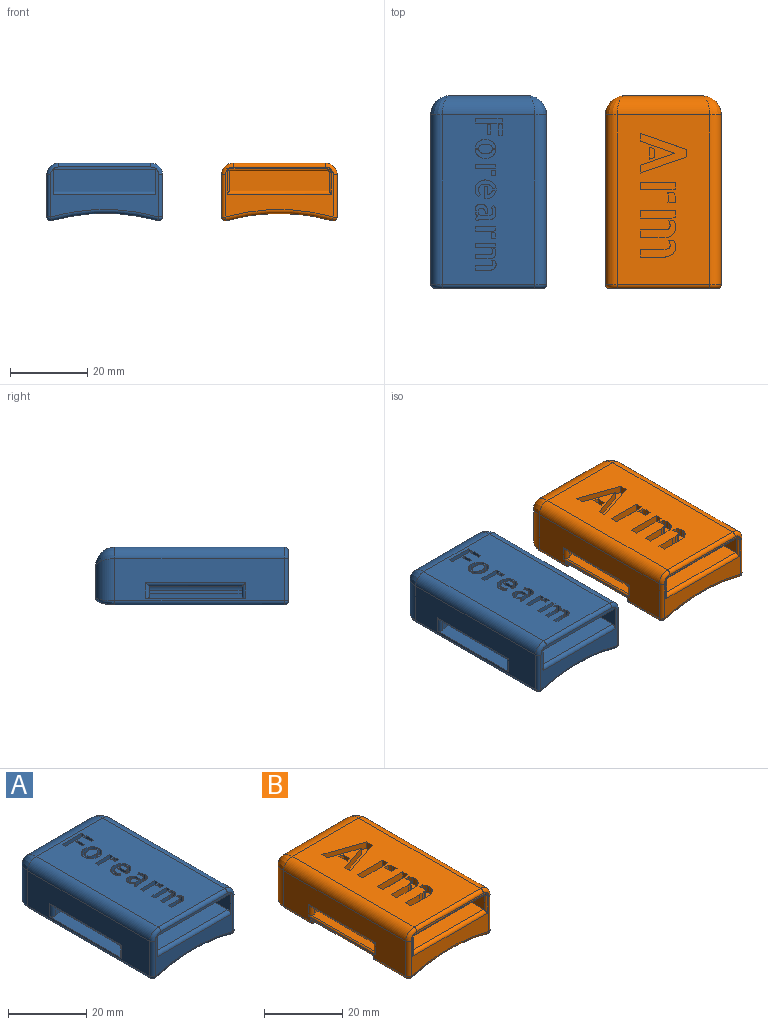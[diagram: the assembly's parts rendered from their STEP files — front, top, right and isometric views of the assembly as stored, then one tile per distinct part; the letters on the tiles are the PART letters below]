
ASSEMBLY  parts=2 mates=2
PART A: 261 faces, bbox 30.7x50x15.5 mm
  f0: cylinder r=50mm len=48mm, axis (0,1,0), area 1052.9mm2, adj f224,f227,f230,f231,f242,f243,f244,f245
  f1: cylinder r=50mm len=26mm, axis (0,1,0), area 125.4mm2, adj f5,f17,f18,f238,f239,f257
  f2: cylinder r=50mm len=24mm, axis (0,1,0), area 3.4mm2, adj f21,f22,f221,f259
  f3: plane 44x24mm, normal (0,0,1), area 969.2mm2, adj f7,f9,f23,f24,f25,f26,f27,f28
  f4: plane 45x26.5mm, normal (0,0,-1), area 1105.7mm2, adj f6,f11,f13,f14,f23,f24,f25,f26
  f5: plane 44x10.96mm, normal (1,0,0), area 375.8mm2, adj f1,f9,f230,f234,f238,f239,f240,f251
  f6: plane 28x12.96mm, normal (0,-1,0), area 152.2mm2, adj f4,f11,f13,f225,f226,f229,f231,f232
  f7: cylinder r=3mm len=44mm, axis (0,1,0), area 207.3mm2, adj f3,f8,f226,f254
  f8: plane 44x10.96mm, normal (-1,0,0), area 375.8mm2, adj f7,f20,f224,f225,f235,f236,f237,f255
  f9: cylinder r=3mm len=44mm, axis (0,1,0), area 207.3mm2, adj f3,f5,f232,f252
  f10: plane 20x7.99mm, normal (0,1,0), area 146.6mm2, adj f227,f251,f253,f255
  f11: plane 45x6.5mm, normal (1,0,0), area 247.7mm2, adj f4,f6,f12,f14,f241
  f12: plane 44x26.5mm, normal (0,0,1), area 1166mm2, adj f11,f13,f14,f241
  f13: plane 45x6.5mm, normal (-1,0,0), area 247.7mm2, adj f4,f6,f12,f14,f241
  f14: plane 26.5x5.5mm, normal (0,-1,0), area 145.7mm2, adj f4,f11,f12,f13
  f15: cylinder r=50mm len=24mm, axis (0,1,0), area 3.4mm2, adj f17,f18,f223,f260
  f16: cylinder r=50mm len=24mm, axis (0,1,0), area 146.8mm2, adj f17,f18,f240,f260
  f17: plane 9.64x4.49mm, normal (0,1,0), area 31mm2, adj f1,f15,f16,f222,f223,f238,f240,f244
  f18: plane 9.64x4.49mm, normal (0,-1,0), area 31mm2, adj f1,f15,f16,f222,f223,f239,f240,f242
  f19: cylinder r=50mm len=24mm, axis (0,1,0), area 146.8mm2, adj f21,f22,f237,f259
  f20: cylinder r=50mm len=26mm, axis (0,1,0), area 125.4mm2, adj f8,f21,f22,f235,f236,f258
  f21: plane 9.64x4.49mm, normal (0,1,0), area 31mm2, adj f2,f19,f20,f220,f221,f235,f237,f248
  f22: plane 9.64x4.49mm, normal (0,-1,0), area 31mm2, adj f2,f19,f20,f220,f221,f236,f237,f246
  f23: plane 1.75x0.55mm, normal (-0.22,0.98,0), area 1mm2, adj f3,f4,f24,f27
  f24: plane 1.75x1.03mm, normal (-1,0,0), area 1.8mm2, adj f3,f4,f23,f25
  f25: plane 5.36x1.75mm, normal (0,-1,0), area 9.4mm2, adj f3,f4,f24,f26
  f26: plane 1.75x1.16mm, normal (1,0,0), area 2mm2, adj f3,f4,f25,f27
  f27: plane 4.81x1.75mm, normal (0,1,0), area 8.4mm2, adj f3,f4,f23,f26
  f28: extruded ~1.75x0.61mm, area 1.1mm2, adj f3,f4,f29,f43
  f29: extruded ~1.75x0.49mm, area 0.9mm2, adj f3,f4,f28,f30
  f30: extruded ~1.75x0.52mm, area 1mm2, adj f3,f4,f29,f31
  f31: plane 1.75x0.75mm, normal (0,-1,0), area 1.3mm2, adj f3,f4,f30,f32
  f32: extruded ~1.75x0.5mm, area 0.9mm2, adj f3,f4,f31,f33
  f33: extruded ~1.75x0.29mm, area 0.5mm2, adj f3,f4,f32,f34
  f34: extruded ~1.75x0.39mm, area 0.7mm2, adj f3,f4,f33,f35
  f35: extruded ~1.75x0.36mm, area 0.7mm2, adj f3,f4,f34,f36
  f36: extruded ~1.75x0.52mm, area 0.9mm2, adj f3,f4,f35,f37
  f37: extruded ~1.75x0.61mm, area 1.1mm2, adj f3,f4,f36,f38
  f38: plane 2.92x1.75mm, normal (0,-1,0), area 5.1mm2, adj f3,f4,f37,f39
  f39: plane 1.75x1.14mm, normal (1,0,0), area 2mm2, adj f3,f4,f38,f40
  f40: plane 3.65x1.75mm, normal (0,1,0), area 6.4mm2, adj f3,f4,f39,f41
  f41: extruded ~1.75x0.71mm, area 1.3mm2, adj f3,f4,f40,f42
  f42: extruded ~1.75x0.57mm, area 1.2mm2, adj f3,f4,f41,f43
  f43: extruded ~1.75x0.5mm, area 1.1mm2, adj f3,f4,f28,f42
  f44: extruded ~1.75x0.36mm, area 0.7mm2, adj f3,f4,f45,f60
  f45: extruded ~1.75x0.59mm, area 1.4mm2, adj f3,f4,f44,f46
  f46: extruded ~1.75x0.74mm, area 1.3mm2, adj f3,f4,f45,f47
  f47: extruded ~1.75x0.52mm, area 0.9mm2, adj f3,f4,f46,f48
  f48: extruded ~1.75x0.49mm, area 0.9mm2, adj f3,f4,f47,f49
  f49: plane 1.75x0.75mm, normal (0,-1,0), area 1.3mm2, adj f3,f4,f48,f50
  f50: extruded ~1.75x0.44mm, area 0.8mm2, adj f3,f4,f49,f51
  f51: extruded ~1.75x0.34mm, area 0.6mm2, adj f3,f4,f50,f52
  f52: extruded ~1.75x0.39mm, area 0.7mm2, adj f3,f4,f51,f53
  f53: extruded ~1.75x0.36mm, area 0.7mm2, adj f3,f4,f52,f54
  f54: extruded ~1.75x0.52mm, area 0.9mm2, adj f3,f4,f53,f55
  f55: plane 3.53x1.75mm, normal (0,-1,0), area 6.2mm2, adj f3,f4,f54,f56
  f56: plane 1.75x1.15mm, normal (1,0,0), area 2mm2, adj f3,f4,f55,f57
  f57: plane 3.01x1.75mm, normal (0,1,0), area 5.3mm2, adj f3,f4,f56,f58
  f58: extruded ~1.75x0.47mm, area 0.8mm2, adj f3,f4,f57,f59
  f59: extruded ~1.75x0.43mm, area 0.8mm2, adj f3,f4,f58,f60
  f60: extruded ~1.75x0.4mm, area 0.7mm2, adj f3,f4,f44,f59
  f61: extruded ~1.75x0.57mm, area 1.1mm2, adj f3,f4,f62,f67
  f62: plane 1.75x0.97mm, normal (0,-1,0), area 1.7mm2, adj f3,f4,f61,f63
  f63: extruded ~1.75x0.4mm, area 0.7mm2, adj f3,f4,f62,f64
  f64: extruded ~1.75x0.42mm, area 0.7mm2, adj f3,f4,f63,f65
  f65: extruded ~1.75x0.65mm, area 1.1mm2, adj f3,f4,f64,f66
  f66: plane 1.75x1.2mm, normal (0,1,0), area 2.1mm2, adj f3,f4,f65,f67
  f67: extruded ~1.75x0.9mm, area 1.6mm2, adj f3,f4,f61,f66
  f68: plane 1.75x0.55mm, normal (-0.22,0.98,0), area 1mm2, adj f3,f4,f69,f72
  f69: plane 1.75x1.03mm, normal (-1,0,0), area 1.8mm2, adj f3,f4,f68,f70
  f70: plane 5.36x1.75mm, normal (0,-1,0), area 9.4mm2, adj f3,f4,f69,f71
  f71: plane 1.75x1.15mm, normal (1,0,0), area 2mm2, adj f3,f4,f70,f72
  f72: plane 4.81x1.75mm, normal (0,1,0), area 8.4mm2, adj f3,f4,f68,f71
  f73: extruded ~1.75x0.64mm, area 1.2mm2, adj f3,f4,f74,f91
  f74: extruded ~1.75x0.5mm, area 0.9mm2, adj f3,f4,f73,f75
  f75: extruded ~1.75x0.3mm, area 0.7mm2, adj f3,f4,f74,f76
  f76: extruded ~1.75x0.39mm, area 0.7mm2, adj f3,f4,f75,f77
  f77: extruded ~1.75x0.4mm, area 0.7mm2, adj f3,f4,f76,f78
  f78: plane 1.75x0.21mm, normal (1,0,0), area 0.4mm2, adj f3,f4,f77,f79
  f79: plane 1.75x0.67mm, normal (0,1,0), area 1.2mm2, adj f3,f4,f78,f80
  f80: plane 1.75x0.42mm, normal (-1,0,0), area 0.7mm2, adj f3,f4,f79,f81
  f81: extruded ~1.75x0.75mm, area 1.3mm2, adj f3,f4,f80,f82
  f82: extruded ~1.75x0.66mm, area 1.3mm2, adj f3,f4,f81,f83
  f83: extruded ~1.75x0.52mm, area 1.2mm2, adj f3,f4,f82,f84
  f84: extruded ~1.75x0.75mm, area 1.4mm2, adj f3,f4,f83,f85
  f85: extruded ~1.75x0.77mm, area 1.4mm2, adj f3,f4,f84,f86
  f86: extruded ~1.75x0.5mm, area 1.1mm2, adj f3,f4,f85,f87
  f87: extruded ~1.75x0.53mm, area 1mm2, adj f3,f4,f86,f88
  f88: extruded ~1.75x0.62mm, area 1.1mm2, adj f3,f4,f87,f89
  f89: extruded ~1.75x0.12mm, area 0.2mm2, adj f3,f4,f88,f90
  f90: plane 1.75x0.77mm, normal (0,1,0), area 1.3mm2, adj f3,f4,f89,f91
  f91: extruded ~1.75x0.51mm, area 1mm2, adj f3,f4,f73,f90
  f92: extruded ~1.75x0.22mm, area 0.4mm2, adj f3,f4,f93,f126
  f93: plane 1.75x1.31mm, normal (0,1,0), area 2.3mm2, adj f3,f4,f92,f94
  f94: extruded ~1.75x0.67mm, area 1.2mm2, adj f3,f4,f93,f95
  f95: extruded ~1.75x0.67mm, area 1.2mm2, adj f3,f4,f94,f96
  f96: extruded ~1.75x0.55mm, area 1.1mm2, adj f3,f4,f95,f97
  f97: extruded ~1.75x0.39mm, area 0.9mm2, adj f3,f4,f96,f98
  f98: extruded ~1.75x0.49mm, area 0.9mm2, adj f3,f4,f97,f99
  f99: extruded ~1.75x0.56mm, area 1mm2, adj f3,f4,f98,f100
  f100: extruded ~1.75x0.6mm, area 1.1mm2, adj f3,f4,f99,f101
  f101: extruded ~1.75x0.54mm, area 1mm2, adj f3,f4,f100,f102
  f102: extruded ~1.75x0.44mm, area 0.8mm2, adj f3,f4,f101,f103
  f103: extruded ~1.75x0.28mm, area 0.6mm2, adj f3,f4,f102,f104
  f104: plane 1.75x0.65mm, normal (0.55,-0.84,0), area 1.4mm2, adj f3,f4,f103,f105
  f105: extruded ~1.75x0.18mm, area 0.4mm2, adj f3,f4,f104,f106
  f106: extruded ~1.75x0.28mm, area 0.6mm2, adj f3,f4,f105,f107
  f107: extruded ~1.75x0.34mm, area 0.6mm2, adj f3,f4,f106,f108
  f108: extruded ~1.75x0.39mm, area 0.7mm2, adj f3,f4,f107,f109
  f109: extruded ~1.75x0.39mm, area 0.7mm2, adj f3,f4,f108,f110
  f110: extruded ~1.75x0.28mm, area 0.6mm2, adj f3,f4,f109,f111
  f111: extruded ~1.75x0.4mm, area 0.8mm2, adj f3,f4,f110,f112
  f112: extruded ~1.75x0.74mm, area 1.3mm2, adj f3,f4,f111,f113
  f113: plane 2x1.75mm, normal (0,-1,0), area 3.5mm2, adj f3,f4,f112,f114
  f114: extruded ~1.75x0.33mm, area 0.8mm2, adj f3,f4,f113,f115
  f115: extruded ~1.75x0.41mm, area 0.8mm2, adj f3,f4,f114,f116
  f116: plane 1.75x0.72mm, normal (0,-1,0), area 1.3mm2, adj f3,f4,f115,f117
  f117: extruded ~1.75x0.62mm, area 1.2mm2, adj f3,f4,f116,f118
  f118: extruded ~1.75x0.42mm, area 1mm2, adj f3,f4,f117,f119
  f119: extruded ~1.75x0.28mm, area 0.5mm2, adj f3,f4,f118,f120
  f120: extruded ~1.75x0.23mm, area 0.6mm2, adj f3,f4,f119,f121
  f121: extruded ~1.75x0.27mm, area 0.5mm2, adj f3,f4,f120,f122
  f122: extruded ~1.75x0.26mm, area 0.5mm2, adj f3,f4,f121,f123
  f123: plane 1.75x0.64mm, normal (0.43,0.9,0), area 1.2mm2, adj f3,f4,f122,f124
  f124: extruded ~1.75x0.17mm, area 0.4mm2, adj f3,f4,f123,f125
  f125: extruded ~1.75x0.28mm, area 0.5mm2, adj f3,f4,f124,f126
  f126: extruded ~1.75x0.3mm, area 0.5mm2, adj f3,f4,f92,f125
  f127: extruded ~1.75x0.93mm, area 1.7mm2, adj f3,f4,f128,f139
  f128: plane 1.75x0.89mm, normal (0,-1,0), area 1.6mm2, adj f3,f4,f127,f129
  f129: extruded ~1.75x0.47mm, area 0.9mm2, adj f3,f4,f128,f130
  f130: extruded ~1.75x0.37mm, area 0.9mm2, adj f3,f4,f129,f131
  f131: extruded ~1.75x0.42mm, area 0.9mm2, adj f3,f4,f130,f132
  f132: extruded ~1.75x0.48mm, area 0.8mm2, adj f3,f4,f131,f133
  f133: plane 2.19x1.75mm, normal (-1,0,0), area 3.8mm2, adj f3,f4,f132,f134
  f134: plane 1.75x0.84mm, normal (0,-1,0), area 1.5mm2, adj f3,f4,f133,f135
  f135: plane 3.26x1.75mm, normal (1,0,0), area 5.7mm2, adj f3,f4,f134,f136
  f136: extruded ~1.75x0.46mm, area 0.8mm2, adj f3,f4,f135,f137
  f137: extruded ~1.75x0.97mm, area 1.7mm2, adj f3,f4,f136,f138
  f138: extruded ~1.75x0.83mm, area 1.7mm2, adj f3,f4,f137,f139
  f139: extruded ~1.75x0.71mm, area 1.6mm2, adj f3,f4,f127,f138
  f140: extruded ~1.75x0.26mm, area 0.5mm2, adj f3,f4,f141,f163
  f141: extruded ~1.75x0.68mm, area 1.2mm2, adj f3,f4,f140,f142
  f142: extruded ~1.75x0.47mm, area 1.1mm2, adj f3,f4,f141,f143
  f143: extruded ~1.75x0.55mm, area 1.1mm2, adj f3,f4,f142,f144
  f144: extruded ~1.75x0.69mm, area 1.2mm2, adj f3,f4,f143,f145
  f145: extruded ~1.75x0.5mm, area 0.9mm2, adj f3,f4,f144,f146
  f146: extruded ~1.75x0.57mm, area 1.1mm2, adj f3,f4,f145,f147
  f147: extruded ~1.75x0.5mm, area 1.1mm2, adj f3,f4,f146,f148
  f148: extruded ~1.75x0.58mm, area 1.1mm2, adj f3,f4,f147,f149
  f149: plane 1.75x0.91mm, normal (0,1,0), area 1.6mm2, adj f3,f4,f148,f150
  f150: extruded ~1.75x0.87mm, area 1.6mm2, adj f3,f4,f149,f151
  f151: extruded ~1.75x0.71mm, area 1.6mm2, adj f3,f4,f150,f152
  f152: extruded ~1.75x0.85mm, area 1.7mm2, adj f3,f4,f151,f153
  f153: extruded ~1.75x1.03mm, area 1.8mm2, adj f3,f4,f152,f154
  f154: extruded ~1.75x1.06mm, area 1.9mm2, adj f3,f4,f153,f155
  f155: extruded ~1.75x0.86mm, area 1.8mm2, adj f3,f4,f154,f156
  f156: extruded ~1.75x0.78mm, area 1.7mm2, adj f3,f4,f155,f157
  f157: extruded ~1.75x0.98mm, area 1.8mm2, adj f3,f4,f156,f158
  f158: extruded ~1.75x1.06mm, area 1.9mm2, adj f3,f4,f157,f159
  f159: extruded ~1.75x0.73mm, area 1.7mm2, adj f3,f4,f158,f160
  f160: plane 1.75x0.64mm, normal (-0.55,0.84,0), area 1.3mm2, adj f3,f4,f159,f161
  f161: extruded ~1.75x0.31mm, area 0.7mm2, adj f3,f4,f160,f162
  f162: extruded ~1.75x0.35mm, area 0.7mm2, adj f3,f4,f161,f163
  f163: extruded ~1.75x0.33mm, area 0.6mm2, adj f3,f4,f140,f162
  f164: extruded ~1.75x0.57mm, area 1.1mm2, adj f3,f4,f165,f170
  f165: plane 1.75x0.97mm, normal (0,-1,0), area 1.7mm2, adj f3,f4,f164,f166
  f166: extruded ~1.75x0.4mm, area 0.7mm2, adj f3,f4,f165,f167
  f167: extruded ~1.75x0.42mm, area 0.7mm2, adj f3,f4,f166,f168
  f168: extruded ~1.75x0.65mm, area 1.1mm2, adj f3,f4,f167,f169
  f169: plane 1.75x1.2mm, normal (0,1,0), area 2.1mm2, adj f3,f4,f168,f170
  f170: extruded ~1.75x0.9mm, area 1.6mm2, adj f3,f4,f164,f169
  f171: plane 1.75x0.55mm, normal (-0.22,0.98,0), area 1mm2, adj f3,f4,f172,f175
  f172: plane 1.75x1.03mm, normal (-1,0,0), area 1.8mm2, adj f3,f4,f171,f173
  f173: plane 5.36x1.75mm, normal (0,-1,0), area 9.4mm2, adj f3,f4,f172,f174
  f174: plane 1.75x1.15mm, normal (1,0,0), area 2mm2, adj f3,f4,f173,f175
  f175: plane 4.81x1.75mm, normal (0,1,0), area 8.4mm2, adj f3,f4,f171,f174
  f176: extruded ~1.75x1.02mm, area 1.8mm2, adj f3,f4,f177,f191
  f177: extruded ~1.75x1.03mm, area 1.8mm2, adj f3,f4,f176,f178
  f178: extruded ~1.75x0.84mm, area 1.7mm2, adj f3,f4,f177,f179
  f179: extruded ~1.75x0.71mm, area 1.6mm2, adj f3,f4,f178,f180
  f180: extruded ~1.75x0.94mm, area 1.7mm2, adj f3,f4,f179,f181
  f181: plane 1.75x0.91mm, normal (0,1,0), area 1.6mm2, adj f3,f4,f180,f182
  f182: extruded ~1.75x0.44mm, area 0.9mm2, adj f3,f4,f181,f183
  f183: extruded ~1.75x0.41mm, area 0.9mm2, adj f3,f4,f182,f184
  f184: extruded ~1.75x0.56mm, area 1mm2, adj f3,f4,f183,f185
  f185: extruded ~1.75x0.66mm, area 1.2mm2, adj f3,f4,f184,f186
  f186: extruded ~1.75x1.19mm, area 2.2mm2, adj f3,f4,f185,f187
  f187: extruded ~1.75x0.76mm, area 1.7mm2, adj f3,f4,f186,f188
  f188: plane 1.75x0.88mm, normal (0,1,0), area 1.5mm2, adj f3,f4,f187,f189
  f189: extruded ~1.75x0.92mm, area 1.7mm2, adj f3,f4,f188,f190
  f190: extruded ~1.75x0.72mm, area 1.6mm2, adj f3,f4,f189,f191
  f191: extruded ~1.75x0.83mm, area 1.7mm2, adj f3,f4,f176,f190
  f192: extruded ~1.75x0.95mm, area 1.7mm2, adj f3,f4,f193,f207
  f193: plane 1.75x0.89mm, normal (0,-1,0), area 1.6mm2, adj f3,f4,f192,f194
  f194: extruded ~1.75x0.45mm, area 0.9mm2, adj f3,f4,f193,f195
  f195: extruded ~1.75x0.41mm, area 0.9mm2, adj f3,f4,f194,f196
  f196: extruded ~1.75x0.56mm, area 1mm2, adj f3,f4,f195,f197
  f197: extruded ~1.75x0.66mm, area 1.2mm2, adj f3,f4,f196,f198
  f198: extruded ~1.75x1.19mm, area 2.2mm2, adj f3,f4,f197,f199
  f199: extruded ~1.75x0.77mm, area 1.8mm2, adj f3,f4,f198,f200
  f200: plane 1.75x0.91mm, normal (0,-1,0), area 1.6mm2, adj f3,f4,f199,f201
  f201: extruded ~1.75x0.93mm, area 1.7mm2, adj f3,f4,f200,f202
  f202: extruded ~1.75x0.72mm, area 1.6mm2, adj f3,f4,f201,f203
  f203: extruded ~1.75x0.84mm, area 1.7mm2, adj f3,f4,f202,f204
  f204: extruded ~1.75x1.03mm, area 1.8mm2, adj f3,f4,f203,f205
  f205: extruded ~1.75x1.04mm, area 1.8mm2, adj f3,f4,f204,f206
  f206: extruded ~1.75x0.85mm, area 1.7mm2, adj f3,f4,f205,f207
  f207: extruded ~1.75x0.72mm, area 1.6mm2, adj f3,f4,f192,f206
  f208: plane 1.75x0.86mm, normal (0,1,0), area 1.5mm2, adj f3,f4,f209,f211
  f209: plane 2.83x1.75mm, normal (-1,0,0), area 4.9mm2, adj f3,f4,f208,f210
  f210: plane 1.75x0.86mm, normal (0,-1,0), area 1.5mm2, adj f3,f4,f209,f211
  f211: plane 2.83x1.75mm, normal (1,0,0), area 4.9mm2, adj f3,f4,f208,f210
  f212: plane 2.53x1.75mm, normal (1,0,0), area 4.4mm2, adj f3,f4,f213,f215
  f213: plane 1.75x0.78mm, normal (0,1,0), area 1.4mm2, adj f3,f4,f212,f214
  f214: plane 2.53x1.75mm, normal (-1,0,0), area 4.4mm2, adj f3,f4,f213,f215
  f215: plane 1.75x0.78mm, normal (0,-1,0), area 1.4mm2, adj f3,f4,f212,f214
  f216: plane 1.75x1.16mm, normal (-1,0,0), area 2mm2, adj f3,f4,f217,f219
  f217: plane 7x1.75mm, normal (0,-1,0), area 12.2mm2, adj f3,f4,f216,f218
  f218: plane 1.75x1.16mm, normal (1,0,0), area 2mm2, adj f3,f4,f217,f219
  f219: plane 7x1.75mm, normal (0,1,0), area 12.2mm2, adj f3,f4,f216,f218
  f220: plane 24.02x0.62mm, normal (1,0,0), area 14.8mm2, adj f21,f22,f246,f247,f249,f258
  f221: plane 24x1.46mm, normal (-1,0,0), area 34.9mm2, adj f2,f21,f22,f248
  f222: plane 24.02x0.62mm, normal (-1,0,0), area 14.8mm2, adj f17,f18,f242,f243,f245,f257
  f223: plane 24x1.46mm, normal (1,0,0), area 34.9mm2, adj f15,f17,f18,f244
  f224: cylinder r=1mm len=44mm, axis (0,1,0), area 81.4mm2, adj f0,f8,f228,f256
  f225: cylinder r=1mm len=10.96mm, axis (0,0,1), area 17.2mm2, adj f6,f8,f226,f228
  f226: torus R=2mm, axis (0,-1,0), area 6.5mm2, adj f6,f7,f225,f229
  f227: torus R=51mm, axis (0,-1,0), area 31.2mm2, adj f0,f10,f250,f256
  f228: sphere r=1mm, area 1.8mm2, adj f224,f225,f231
  f229: cylinder r=1mm len=24mm, axis (1,0,0), area 37.7mm2, adj f3,f6,f226,f232
  f230: cylinder r=1mm len=44mm, axis (0,1,0), area 81.4mm2, adj f0,f5,f233,f250
  f231: torus R=51mm, axis (0,-1,0), area 44mm2, adj f0,f6,f228,f233
  f232: torus R=2mm, axis (0,-1,0), area 6.5mm2, adj f6,f9,f229,f234
  f233: sphere r=1mm, area 1.8mm2, adj f230,f231,f234
  f234: cylinder r=1mm len=10.96mm, axis (0,0,-1), area 17.2mm2, adj f5,f6,f232,f233
  f235: cylinder r=1mm len=4.09mm, axis (0,0,-1), area 5.3mm2, adj f8,f20,f21,f237
  f236: cylinder r=1mm len=4.09mm, axis (0,0,1), area 5.3mm2, adj f8,f20,f22,f237
  f237: cylinder r=1mm len=26mm, axis (0,1,0), area 45.5mm2, adj f8,f19,f21,f22,f235,f236
  f238: cylinder r=1mm len=4.09mm, axis (0,0,-1), area 5.3mm2, adj f1,f5,f17,f240
  f239: cylinder r=1mm len=4.09mm, axis (0,0,1), area 5.3mm2, adj f1,f5,f18,f240
  f240: cylinder r=1mm len=26mm, axis (0,1,0), area 45.5mm2, adj f5,f16,f17,f18,f238,f239
  f241: cylinder r=1mm len=26.5mm, axis (-1,0,0), area 41.6mm2, adj f6,f11,f12,f13
  f242: torus R=50.5mm, axis (0,-1,0), area 3.8mm2, adj f0,f18,f222,f243,f244
  f243: cylinder r=0.5mm len=25mm, axis (0,1,0), area 16.9mm2, adj f0,f222,f242,f245
  f244: cylinder r=0.5mm len=25mm, axis (0,1,0), area 20.1mm2, adj f0,f17,f18,f223,f242,f245
  f245: torus R=50.5mm, axis (0,-1,0), area 3.8mm2, adj f0,f17,f222,f243,f244
  f246: torus R=50.5mm, axis (0,-1,0), area 3.8mm2, adj f0,f22,f220,f247,f248
  f247: cylinder r=0.5mm len=25mm, axis (0,1,0), area 16.9mm2, adj f0,f220,f246,f249
  f248: cylinder r=0.5mm len=25mm, axis (0,1,0), area 20.1mm2, adj f0,f21,f22,f221,f246,f249
  f249: torus R=50.5mm, axis (0,-1,0), area 3.8mm2, adj f0,f21,f220,f247,f248
  f250: bspline ~6.29x6.07mm, area 12.8mm2, adj f0,f227,f230,f251
  f251: cylinder r=5mm len=10.96mm, axis (0,0,1), area 77.4mm2, adj f5,f10,f250,f252
  f252: bspline ~6.03x5mm, area 24.5mm2, adj f9,f251,f253
  f253: cylinder r=5mm len=24mm, axis (-1,0,0), area 177.1mm2, adj f3,f10,f252,f254
  f254: bspline ~6.03x5mm, area 24.5mm2, adj f7,f253,f255
  f255: cylinder r=5mm len=10.96mm, axis (0,0,-1), area 77.4mm2, adj f8,f10,f254,f256
  f256: bspline ~6.18x5.52mm, area 12.8mm2, adj f0,f224,f227,f255
  f257: cylinder r=0.8mm len=24mm, axis (0,1,0), area 34mm2, adj f1,f17,f18,f222
  f258: cylinder r=0.8mm len=24mm, axis (0,1,0), area 34mm2, adj f20,f21,f22,f220
  f259: cylinder r=3mm len=24mm, axis (0,1,0), area 109.1mm2, adj f2,f19,f21,f22
  f260: cylinder r=3mm len=24mm, axis (0,1,0), area 109.1mm2, adj f15,f16,f17,f18
PART B: 153 faces, bbox 30.7x50.1x15.5 mm
  f0: cylinder r=50mm len=48mm, axis (0,1,0), area 975.9mm2, adj f91,f96,f97,f101,f102,f103,f118,f119
  f1: plane 28x5.04mm, normal (0,1,0), area 57.3mm2, adj f6,f7,f8,f9,f22,f86,f87,f88
  f2: plane 3.1x0.71mm, normal (0,1,0), area 1.1mm2, adj f90,f127,f128,f129,f147
  f3: plane 3.1x0.71mm, normal (0,-1,0), area 1.1mm2, adj f89,f120,f121,f122,f150
  f4: plane 28x5.54mm, normal (0,-1,0), area 71.5mm2, adj f6,f7,f8,f9,f21,f22,f86,f87
  f5: plane 44x10.96mm, normal (1,0,0), area 371.1mm2, adj f15,f96,f100,f101,f107,f108,f109,f123
  f6: plane 22x1mm, normal (-1,0,0), area 22.1mm2, adj f1,f4,f148,f152
  f7: plane 22x1mm, normal (1,0,0), area 22.1mm2, adj f1,f4,f149,f151
  f8: cylinder r=50mm len=22.47mm, axis (0,1,0), area 83.7mm2, adj f1,f4,f104,f105,f131,f151
  f9: cylinder r=50mm len=22.47mm, axis (0,1,0), area 83.7mm2, adj f1,f4,f107,f108,f132,f152
  f10: plane 44x24mm, normal (0,0,1), area 925.8mm2, adj f13,f15,f25,f26,f27,f28,f29,f30
  f11: plane 44.5x25.5mm, normal (0,0,-1), area 1004.5mm2, adj f17,f20,f25,f26,f27,f28,f29,f30
  f12: plane 28x12.96mm, normal (0,-1,0), area 149.2mm2, adj f92,f93,f95,f97,f98,f100,f110,f134
  f13: cylinder r=3mm len=44mm, axis (0,1,0), area 207.3mm2, adj f10,f14,f93,f144
  f14: plane 44x10.96mm, normal (-1,0,0), area 371.1mm2, adj f13,f91,f92,f103,f104,f105,f106,f116
  f15: cylinder r=3mm len=44mm, axis (0,1,0), area 207.3mm2, adj f5,f10,f98,f142
  f16: plane 20x7.99mm, normal (0,1,0), area 146.6mm2, adj f102,f141,f143,f145
  f17: plane 44.5x5.13mm, normal (1,0,0), area 222.5mm2, adj f11,f18,f20,f110,f134
  f18: plane 44x26mm, normal (0,0,1), area 1144mm2, adj f17,f19,f20,f110
  f19: plane 44.5x4.63mm, normal (-1,0,0), area 200.3mm2, adj f18,f20,f110,f137,f139
  f20: plane 26x5mm, normal (0,-1,0), area 129.9mm2, adj f11,f17,f18,f19,f139
  f21: cylinder r=50mm len=27.45mm, axis (0,1,0), area 597.9mm2, adj f4,f106,f109,f113
  f22: cylinder r=50mm len=22mm, axis (0,1,0), area 311.4mm2, adj f1,f4,f87,f130
  f23: plane 3.1x0.71mm, normal (0,1,0), area 1.1mm2, adj f89,f116,f117,f118,f150
  f24: plane 3.1x0.71mm, normal (0,-1,0), area 1.1mm2, adj f90,f123,f124,f125,f147
  f25: plane 2.02x2mm, normal (1,0,0), area 4mm2, adj f10,f11,f26,f31
  f26: plane 11.98x4.17mm, normal (-0.33,0.94,0), area 25.4mm2, adj f10,f11,f25,f27
  f27: plane 2x1.94mm, normal (-1,0,0), area 3.9mm2, adj f10,f11,f26,f28
  f28: plane 11.98x4.2mm, normal (-0.33,-0.94,0), area 25.4mm2, adj f10,f11,f27,f29
  f29: plane 2.03x2mm, normal (1,0,0), area 4.1mm2, adj f10,f11,f28,f30
  f30: plane 8.98x3.14mm, normal (0.33,0.94,0), area 19mm2, adj f10,f11,f29,f31
  f31: plane 8.98x3.11mm, normal (0.33,-0.95,0), area 19mm2, adj f10,f11,f25,f30
  f32: plane 2x1.32mm, normal (-0.34,0.94,0), area 2.8mm2, adj f10,f11,f33,f35
  f33: plane 2.18x2mm, normal (-1,0,0), area 4.4mm2, adj f10,f11,f32,f34
  f34: plane 2x1.32mm, normal (-0.33,-0.95,0), area 2.8mm2, adj f10,f11,f33,f35
  f35: plane 3.11x2mm, normal (1,0,0), area 6.2mm2, adj f10,f11,f32,f34
  f36: plane 2x0.94mm, normal (-0.22,0.98,0), area 1.9mm2, adj f10,f11,f37,f40
  f37: plane 2x1.76mm, normal (-1,0,0), area 3.5mm2, adj f10,f11,f36,f38
  f38: plane 9.18x2mm, normal (0,-1,0), area 18.4mm2, adj f10,f11,f37,f39
  f39: plane 2x1.97mm, normal (1,0,0), area 3.9mm2, adj f10,f11,f38,f40
  f40: plane 8.24x2mm, normal (0,1,0), area 16.5mm2, adj f10,f11,f36,f39
  f41: extruded ~2x0.98mm, area 2.1mm2, adj f10,f11,f42,f47
  f42: plane 2x1.66mm, normal (0,-1,0), area 3.3mm2, adj f10,f11,f41,f43
  f43: extruded ~2x0.69mm, area 1.4mm2, adj f10,f11,f42,f44
  f44: extruded ~2x0.73mm, area 1.5mm2, adj f10,f11,f43,f45
  f45: extruded ~2x1.11mm, area 2.2mm2, adj f10,f11,f44,f46
  f46: plane 2.05x2mm, normal (0,1,0), area 4.1mm2, adj f10,f11,f45,f47
  f47: extruded ~2x1.55mm, area 3.1mm2, adj f10,f11,f41,f46
  f48: plane 2x0.94mm, normal (-0.22,0.98,0), area 1.9mm2, adj f10,f11,f49,f52
  f49: plane 2x1.77mm, normal (-1,0,0), area 3.5mm2, adj f10,f11,f48,f50
  f50: plane 9.18x2mm, normal (0,-1,0), area 18.4mm2, adj f10,f11,f49,f51
  f51: plane 2x1.98mm, normal (1,0,0), area 4mm2, adj f10,f11,f50,f52
  f52: plane 8.24x2mm, normal (0,1,0), area 16.5mm2, adj f10,f11,f48,f51
  f53: extruded ~2x1.04mm, area 2.1mm2, adj f10,f11,f54,f68
  f54: extruded ~2x0.85mm, area 1.7mm2, adj f10,f11,f53,f55
  f55: extruded ~2x0.9mm, area 2mm2, adj f10,f11,f54,f56
  f56: plane 2x1.29mm, normal (0,-1,0), area 2.6mm2, adj f10,f11,f55,f57
  f57: extruded ~2x0.86mm, area 1.8mm2, adj f10,f11,f56,f58
  f58: extruded ~2x0.49mm, area 1mm2, adj f10,f11,f57,f59
  f59: extruded ~2x0.68mm, area 1.5mm2, adj f10,f11,f58,f60
  f60: extruded ~2x0.61mm, area 1.4mm2, adj f10,f11,f59,f61
  f61: extruded ~2x0.89mm, area 1.8mm2, adj f10,f11,f60,f62
  f62: extruded ~2x1.05mm, area 2.1mm2, adj f10,f11,f61,f63
  f63: plane 5x2mm, normal (0,-1,0), area 10mm2, adj f10,f11,f62,f64
  f64: plane 2x1.95mm, normal (1,0,0), area 3.9mm2, adj f10,f11,f63,f65
  f65: plane 6.25x2mm, normal (0,1,0), area 12.5mm2, adj f10,f11,f64,f66
  f66: extruded ~2x1.21mm, area 2.5mm2, adj f10,f11,f65,f67
  f67: extruded ~2x0.97mm, area 2.3mm2, adj f10,f11,f66,f68
  f68: extruded ~2x0.86mm, area 2.1mm2, adj f10,f11,f53,f67
  f69: extruded ~2x0.63mm, area 1.4mm2, adj f10,f11,f70,f85
  f70: extruded ~2x1mm, area 2.7mm2, adj f10,f11,f69,f71
  f71: extruded ~2x1.26mm, area 2.6mm2, adj f10,f11,f70,f72
  f72: extruded ~2x0.89mm, area 1.8mm2, adj f10,f11,f71,f73
  f73: extruded ~2x0.84mm, area 1.8mm2, adj f10,f11,f72,f74
  f74: plane 2x1.29mm, normal (0,-1,0), area 2.6mm2, adj f10,f11,f73,f75
  f75: extruded ~2x0.76mm, area 1.6mm2, adj f10,f11,f74,f76
  f76: extruded ~2x0.58mm, area 1.2mm2, adj f10,f11,f75,f77
  f77: extruded ~2x0.67mm, area 1.4mm2, adj f10,f11,f76,f78
  f78: extruded ~2x0.61mm, area 1.4mm2, adj f10,f11,f77,f79
  f79: extruded ~2x0.89mm, area 1.8mm2, adj f10,f11,f78,f80
  f80: plane 6.05x2mm, normal (0,-1,0), area 12.1mm2, adj f10,f11,f79,f81
  f81: plane 2x1.97mm, normal (1,0,0), area 3.9mm2, adj f10,f11,f80,f82
  f82: plane 5.16x2mm, normal (0,1,0), area 10.3mm2, adj f10,f11,f81,f83
  f83: extruded ~2x0.81mm, area 1.6mm2, adj f10,f11,f82,f84
  f84: extruded ~2x0.74mm, area 1.5mm2, adj f10,f11,f83,f85
  f85: extruded ~2x0.69mm, area 1.4mm2, adj f10,f11,f69,f84
  f86: plane 22x2.2mm, normal (1,0,0), area 48.3mm2, adj f1,f4,f126,f130
  f87: plane 22x0.05mm, normal (0,0,-1), area 1.2mm2, adj f1,f4,f22,f88
  f88: plane 22x2.42mm, normal (-1,0,0), area 53.2mm2, adj f1,f4,f87,f119
  f89: plane 22.04x3.4mm, normal (0,0,-1), area 74.8mm2, adj f3,f23,f118,f120,f149,f150
  f90: plane 22.04x3.4mm, normal (0,0,-1), area 74.8mm2, adj f2,f24,f125,f127,f147,f148
  f91: cylinder r=1mm len=11.5mm, axis (0,1,0), area 21.3mm2, adj f0,f14,f94,f117
  f92: cylinder r=1mm len=10.96mm, axis (0,0,1), area 17.2mm2, adj f12,f14,f93,f94
  f93: torus R=2mm, axis (0,-1,0), area 6.5mm2, adj f12,f13,f92,f95,f133,f135
  f94: sphere r=1mm, area 1.8mm2, adj f91,f92,f97
  f95: cylinder r=1mm len=24mm, axis (1,0,0), area 37.7mm2, adj f10,f12,f93,f98
  f96: cylinder r=1mm len=11.5mm, axis (0,1,0), area 21.3mm2, adj f0,f5,f99,f128
  f97: torus R=51mm, axis (0,-1,0), area 44mm2, adj f0,f12,f94,f99
  f98: torus R=2mm, axis (0,-1,0), area 6.5mm2, adj f12,f15,f95,f100
  f99: sphere r=1mm, area 1.8mm2, adj f96,f97,f100
  f100: cylinder r=1mm len=10.96mm, axis (0,0,-1), area 17.2mm2, adj f5,f12,f98,f99
  f101: cylinder r=1mm len=9.5mm, axis (0,1,0), area 17.6mm2, adj f0,f5,f124,f140
  f102: torus R=51mm, axis (0,-1,0), area 31.2mm2, adj f0,f16,f140,f146
  f103: cylinder r=1mm len=9.5mm, axis (0,1,0), area 17.6mm2, adj f0,f14,f121,f146
  f104: cylinder r=1mm len=3.71mm, axis (0,0,-1), area 4mm2, adj f1,f8,f14,f111,f131
  f105: cylinder r=1mm len=3.71mm, axis (0,0,1), area 4.4mm2, adj f4,f8,f14,f106,f131
  f106: cylinder r=1mm len=24mm, axis (0,1,0), area 41.2mm2, adj f4,f14,f21,f105,f111,f112
  f107: cylinder r=1mm len=3.71mm, axis (0,0,-1), area 4mm2, adj f1,f5,f9,f115,f132
  f108: cylinder r=1mm len=3.71mm, axis (0,0,1), area 4.4mm2, adj f4,f5,f9,f109,f132
  f109: cylinder r=1mm len=24mm, axis (0,1,0), area 41.2mm2, adj f4,f5,f21,f108,f114,f115
  f110: cylinder r=1mm len=27mm, axis (-1,0,0), area 41.4mm2, adj f12,f17,f18,f19,f134,f137
  f111: bspline ~1.5x1.5mm, area 0.5mm2, adj f104,f106,f112
  f112: torus R=1.5mm, axis (0,-1,0), area 0.3mm2, adj f1,f106,f111,f113
  f113: torus R=49.5mm, axis (0,-1,0), area 21.8mm2, adj f1,f21,f112,f114
  f114: torus R=1.5mm, axis (0,-1,0), area 0.3mm2, adj f1,f109,f113,f115
  f115: bspline ~1.5x1.5mm, area 0.5mm2, adj f107,f109,f114
  f116: cylinder r=0.5mm len=0.96mm, axis (0,0,1), area 0.5mm2, adj f14,f23,f117,f150
  f117: torus R=0.5mm, axis (0,-1,0), area 1.2mm2, adj f23,f91,f116,f118
  f118: torus R=50.5mm, axis (0,-1,0), area 5.6mm2, adj f0,f1,f23,f89,f117,f119,f149
  f119: cylinder r=0.5mm len=23mm, axis (0,1,0), area 19mm2, adj f0,f1,f4,f88,f118,f120
  f120: torus R=50.5mm, axis (0,-1,0), area 5.6mm2, adj f0,f3,f4,f89,f119,f121,f149
  f121: torus R=0.5mm, axis (0,-1,0), area 1.2mm2, adj f3,f103,f120,f122
  f122: cylinder r=0.5mm len=0.96mm, axis (0,0,-1), area 0.5mm2, adj f3,f14,f121,f150
  f123: cylinder r=0.5mm len=0.96mm, axis (0,0,-1), area 0.5mm2, adj f5,f24,f124,f147
  f124: torus R=0.5mm, axis (0,-1,0), area 1.2mm2, adj f24,f101,f123,f125
  f125: torus R=50.5mm, axis (0,-1,0), area 5.6mm2, adj f0,f4,f24,f90,f124,f126,f148
  f126: cylinder r=0.5mm len=23mm, axis (0,1,0), area 19mm2, adj f0,f1,f4,f86,f125,f127
  f127: torus R=50.5mm, axis (0,-1,0), area 5.6mm2, adj f0,f1,f2,f90,f126,f128,f148
  f128: torus R=0.5mm, axis (0,-1,0), area 1.2mm2, adj f2,f96,f127,f129
  f129: cylinder r=0.5mm len=0.96mm, axis (0,0,1), area 0.5mm2, adj f2,f5,f128,f147
  f130: cylinder r=0.5mm len=22mm, axis (0,1,0), area 5.1mm2, adj f1,f4,f22,f86
  f131: cylinder r=0.5mm len=24mm, axis (0,1,0), area 14.8mm2, adj f8,f14,f104,f105
  f132: cylinder r=0.5mm len=24mm, axis (0,1,0), area 14.8mm2, adj f5,f9,f107,f108
  f133: bspline ~0.96x0.66mm, area 0mm2, adj f93,f134,f135
  f134: cylinder r=0.5mm len=6.32mm, axis (0,0,1), area 4.5mm2, adj f12,f17,f110,f133,f136
  f135: bspline ~0.96x0.66mm, area 0mm2, adj f93,f133,f136
  f136: cylinder r=0.5mm len=25.82mm, axis (1,0,0), area 20.2mm2, adj f11,f12,f134,f135,f138
  f137: cylinder r=0.5mm len=5.5mm, axis (0,0,-1), area 4mm2, adj f12,f19,f110,f138
  f138: torus R=1mm, axis (0,-1,0), area 0.8mm2, adj f12,f136,f137,f139
  f139: cylinder r=0.5mm len=44.5mm, axis (0,1,0), area 35mm2, adj f11,f19,f20,f138
  f140: bspline ~6.29x6.07mm, area 12.8mm2, adj f0,f101,f102,f141
  f141: cylinder r=5mm len=10.96mm, axis (0,0,1), area 74.4mm2, adj f5,f16,f140,f142
  f142: bspline ~5.26x5mm, area 16.3mm2, adj f15,f141,f143
  f143: cylinder r=5mm len=24mm, axis (-1,0,0), area 172.8mm2, adj f10,f16,f142,f144
  f144: bspline ~5.26x5mm, area 16.3mm2, adj f13,f143,f145
  f145: cylinder r=5mm len=10.96mm, axis (0,0,-1), area 74.4mm2, adj f14,f16,f144,f146
  f146: bspline ~6.18x5.52mm, area 12.8mm2, adj f0,f102,f103,f145
  f147: cylinder r=0.8mm len=23mm, axis (0,1,0), area 28.1mm2, adj f2,f5,f24,f90,f123,f129
  f148: cylinder r=0.8mm len=22.04mm, axis (0,-1,0), area 27.7mm2, adj f1,f4,f6,f90,f125,f127
  f149: cylinder r=0.8mm len=22.04mm, axis (0,1,0), area 27.7mm2, adj f1,f4,f7,f89,f118,f120
  f150: cylinder r=0.8mm len=23mm, axis (0,1,0), area 28.1mm2, adj f3,f14,f23,f89,f116,f122
  f151: cylinder r=0.8mm len=22mm, axis (0,1,0), area 31.5mm2, adj f1,f4,f7,f8
  f152: cylinder r=0.8mm len=22mm, axis (0,1,0), area 31.5mm2, adj f1,f4,f6,f9
PLACE A t=(-51.19,11.7,-3.51)mm
PLACE B t=(-5.88,11.66,-3.53)mm
MATE parallel B.f16 <-> A.f10  axis (0,1,0) through (-15.88,11.66,-8.02)mm
MATE parallel A.f3 <-> B.f10  axis (0,0,1) through (-51.14,-15.42,0.99)mm
